# Revit family: EZTA (24x16) with Hot Water Coil
name_source: partatom
category: Mechanical Equipment
revit_build: Autodesk Revit 2016 (Build: 20150714_1515(x64)
units: mm (PartAtom-declared; Revit-internal decimal feet)

## family parameters
Always vertical = Yes
Cut with Voids When Loaded = No
Part Type = Normal
Room Calculation Point = No
Round Connector Dimension = Use Radius
Shared = No
Work Plane-Based = No

## types (2) — shared parameters
Duct Discharge Height = 18"
Duct Discharge Width = 38"
Duct Inlet Height = 16"
Duct Inlet Width = 24"
HWC Conn "B" = 1 3/4"
HWC Conn "D" = 17/32"
HWC Conn "E" = 1 5/32"
HWC Conn Diameter = 1"
HWC Conn Radius = 0"
HWC Depth "A" = 7"
Height = 18"
Length = 39 1/2"
Manufacturer = Anemostat
Model = EZTS With Hot Water Coil
URL = http://www.anemostat.com
Width = 38"

## per-type parameters (varying)
| type | HWC Conn "C" |
| EZTS - 24x16 with 1 Row Hot Water Coil | 3 1/4" |
| EZTS - 24x16 with 2 Row Hot Water Coil | 2 27/32" |

## geometry (parser evidence)
native form markers: Sweep x3
no freeform markers — native parametric forms only
